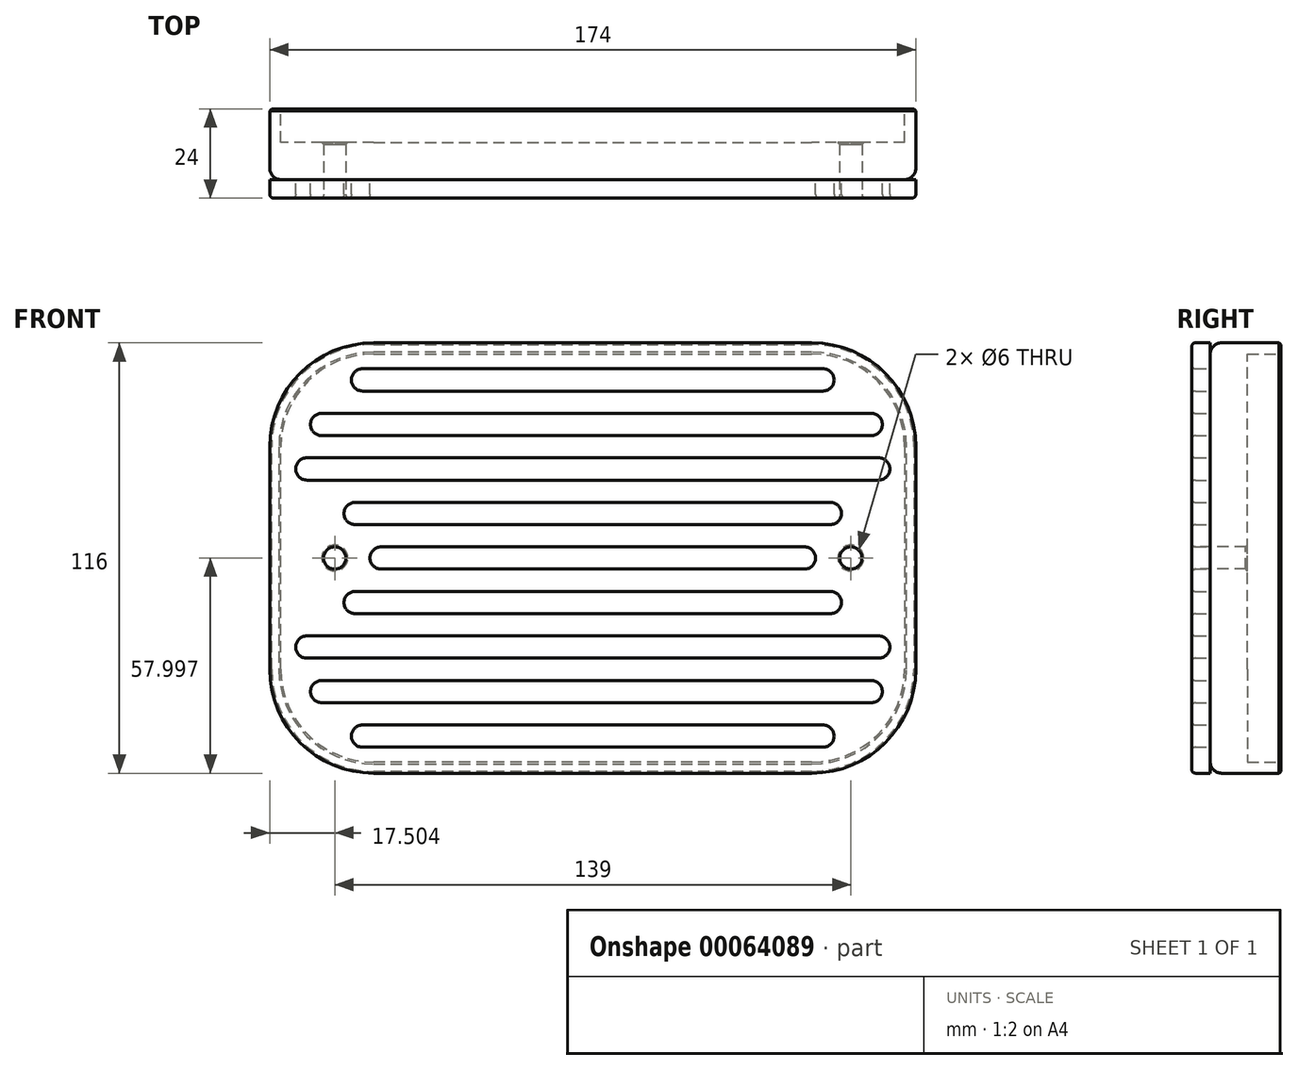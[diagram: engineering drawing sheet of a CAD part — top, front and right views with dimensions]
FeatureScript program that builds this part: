
annotation { "Feature Type Name" : "Feature", "Feature Type Description" : "" }
export const myFeature = defineFeature(function(context is Context, id is Id, definition is map)
    precondition{}
    {
        {
            var Q0;
            Q0=qCreatedBy(makeId("Front.planeOp"),FACE);
            var sketch = newSketch(context, id + "F0", { "sketchPlane" : qUnion([Q0])});
            skLineSegment(sketch, "E0.bottom", {"start": v(-55.39, -93.65) * mm, "end": v(62.61, -93.65) * mm});
            skLineSegment(sketch, "E0.top", {"start": v(-55.39, 16.35) * mm, "end": v(62.61, 16.35) * mm});
            skLineSegment(sketch, "E0.left", {"start": v(-80.39, -68.65) * mm, "end": v(-80.39, -8.65) * mm});
            skLineSegment(sketch, "E0.right", {"start": v(87.61, -68.65) * mm, "end": v(87.61, -8.65) * mm});
            skPoint(sketch, "E1.visualSharp", {"position": v(-80.39, 16.35) * mm});
            skArc(sketch, "E1.filletArc", {"start": v(-55.39, 16.35) * mm, "mid": v(-73.06, 9.02) * mm, "end": v(-80.39, -8.65) * mm});
            skPoint(sketch, "E2.visualSharp", {"position": v(87.61, 16.35) * mm});
            skArc(sketch, "E2.filletArc", {"start": v(87.61, -8.65) * mm, "mid": v(80.3, 9.02) * mm, "end": v(62.61, 16.35) * mm});
            skPoint(sketch, "E3.visualSharp", {"position": v(87.61, -93.65) * mm});
            skArc(sketch, "E3.filletArc", {"start": v(62.61, -93.65) * mm, "mid": v(80.3, -86.33) * mm, "end": v(87.61, -68.65) * mm});
            skPoint(sketch, "E4.visualSharp", {"position": v(-80.39, -93.65) * mm});
            skArc(sketch, "E4.filletArc", {"start": v(-80.39, -68.65) * mm, "mid": v(-73.06, -86.33) * mm, "end": v(-55.39, -93.65) * mm});
            skLineSegment(sketch, "E5.0", {"start": v(-55.39, 19.35) * mm, "end": v(62.61, 19.35) * mm});
            skArc(sketch, "E6.0", {"start": v(90.61, -8.65) * mm, "mid": v(82.41, 11.15) * mm, "end": v(62.61, 19.35) * mm});
            skLineSegment(sketch, "E6.1", {"start": v(90.61, -68.65) * mm, "end": v(90.61, -8.65) * mm});
            skArc(sketch, "E6.2", {"start": v(62.61, -96.65) * mm, "mid": v(82.41, -88.45) * mm, "end": v(90.61, -68.65) * mm});
            skArc(sketch, "E6.3", {"start": v(-55.39, 19.35) * mm, "mid": v(-75.19, 11.15) * mm, "end": v(-83.39, -8.65) * mm});
            skLineSegment(sketch, "E6.4", {"start": v(-83.39, -68.65) * mm, "end": v(-83.39, -8.65) * mm});
            skArc(sketch, "E6.5", {"start": v(-83.39, -68.65) * mm, "mid": v(-75.19, -88.45) * mm, "end": v(-55.39, -96.65) * mm});
            skLineSegment(sketch, "E6.6", {"start": v(-55.39, -96.65) * mm, "end": v(62.61, -96.65) * mm});
            skSolve(sketch);
        }
        {
            var Q0;
            Q0=makeQuery(id+"F0.imprint","IMPRINT",FACE,{"disambiguationData":[TD([[makeQuery(id+"F0.imprint","IMPRINT",EDGE,{"derivedFrom":sQuery(id+"F0.wireOp",EDGE,"E0.bottom")}),1.0]])]});
            var Q1;
            Q1=makeQuery(id+"F0.imprint","IMPRINT",FACE,{"disambiguationData":[TD([[makeQuery(id+"F0.imprint","IMPRINT",EDGE,{"derivedFrom":sQuery(id+"F0.wireOp",EDGE,"E0.bottom")}),-1.0]])]});
            extrude(context, id + "F1", {"entities" : qUnion([Q0, Q1]), "depth" : 19 * mm});
        }
        {
            var Q0;
            Q0=makeQuery(id+"F0.imprint","IMPRINT",FACE,{"disambiguationData":[TD([[makeQuery(id+"F0.imprint","IMPRINT",EDGE,{"derivedFrom":sQuery(id+"F0.wireOp",EDGE,"E0.bottom")}),1.0]])]});
            extrude(context, id + "F2", {"entities" : qUnion([Q0]), "operationType" : NewBodyOperationType.REMOVE, "depth" : 9 * mm});
        }
        {
            var Q0;
            Q0=makeQuery(id+"F1.opExtrude","CAP_FACE",FACE,{"disambiguationData":[OSD([sQuery(id+"F0.wireOp",EDGE,"E5.0"),sQuery(id+"F0.wireOp",EDGE,"E6.0"),sQuery(id+"F0.wireOp",EDGE,"E6.1"),sQuery(id+"F0.wireOp",EDGE,"E6.2"),sQuery(id+"F0.wireOp",EDGE,"E6.3"),sQuery(id+"F0.wireOp",EDGE,"E6.4"),sQuery(id+"F0.wireOp",EDGE,"E6.5"),sQuery(id+"F0.wireOp",EDGE,"E6.6")])],"isStart":false});
            var sketch = newSketch(context, id + "F3", { "sketchPlane" : qUnion([Q0])});
            skCircle(sketch, "E7", {"center": v(-65.89, -38.65) * mm, "radius": 3 * mm});
            skCircle(sketch, "E8", {"center": v(73.11, -38.65) * mm, "radius": 3 * mm});
            skLineSegment(sketch, "E9", {"start": v(-53.39, -38.65) * mm, "end": v(60.61, -38.65) * mm});
            skLineSegment(sketch, "E10.0", {"start": v(-60.39, -26.65) * mm, "end": v(67.61, -26.65) * mm});
            skLineSegment(sketch, "E11.0", {"start": v(-73.39, -14.65) * mm, "end": v(80.61, -14.65) * mm});
            skLineSegment(sketch, "E12.0", {"start": v(-69.39, -2.65) * mm, "end": v(78.61, -2.65) * mm});
            skLineSegment(sketch, "E13.0", {"start": v(-58.39, 9.35) * mm, "end": v(65.61, 9.35) * mm});
            skLineSegment(sketch, "E14.MirrorCS", {"start": v(-60.39, -50.65) * mm, "end": v(67.61, -50.65) * mm});
            skLineSegment(sketch, "E15.MirrorCS", {"start": v(-73.39, -62.65) * mm, "end": v(80.61, -62.65) * mm});
            skLineSegment(sketch, "E16.MirrorCS", {"start": v(-69.39, -74.65) * mm, "end": v(78.61, -74.65) * mm});
            skLineSegment(sketch, "E17.MirrorCS", {"start": v(-58.39, -86.65) * mm, "end": v(65.61, -86.65) * mm});
            skArc(sketch, "E18.0.startCap", {"start": v(-69.39, -5.65) * mm, "mid": v(-72.39, -2.65) * mm, "end": v(-69.39, 0.35) * mm});
            skArc(sketch, "E18.0.endCap", {"start": v(78.61, 0.35) * mm, "mid": v(81.61, -2.65) * mm, "end": v(78.61, -5.65) * mm});
            skLineSegment(sketch, "E18.0.left", {"start": v(-69.39, 0.35) * mm, "end": v(78.61, 0.35) * mm});
            skLineSegment(sketch, "E18.0.right", {"start": v(-69.39, -5.65) * mm, "end": v(78.61, -5.65) * mm});
            skArc(sketch, "E18.1.startCap", {"start": v(-73.39, -17.65) * mm, "mid": v(-76.39, -14.65) * mm, "end": v(-73.39, -11.65) * mm});
            skArc(sketch, "E18.1.endCap", {"start": v(80.61, -11.65) * mm, "mid": v(83.61, -14.65) * mm, "end": v(80.61, -17.65) * mm});
            skLineSegment(sketch, "E18.1.left", {"start": v(-73.39, -11.65) * mm, "end": v(80.61, -11.65) * mm});
            skLineSegment(sketch, "E18.1.right", {"start": v(-73.39, -17.65) * mm, "end": v(80.61, -17.65) * mm});
            skArc(sketch, "E18.2.startCap", {"start": v(-60.39, -29.65) * mm, "mid": v(-63.39, -26.65) * mm, "end": v(-60.39, -23.65) * mm});
            skArc(sketch, "E18.2.endCap", {"start": v(67.61, -23.65) * mm, "mid": v(70.61, -26.65) * mm, "end": v(67.61, -29.65) * mm});
            skLineSegment(sketch, "E18.2.left", {"start": v(-60.39, -23.65) * mm, "end": v(67.61, -23.65) * mm});
            skLineSegment(sketch, "E18.2.right", {"start": v(-60.39, -29.65) * mm, "end": v(67.61, -29.65) * mm});
            skArc(sketch, "E18.3.startCap", {"start": v(-53.39, -41.65) * mm, "mid": v(-56.39, -38.65) * mm, "end": v(-53.39, -35.65) * mm});
            skArc(sketch, "E18.3.endCap", {"start": v(60.61, -35.65) * mm, "mid": v(63.61, -38.65) * mm, "end": v(60.61, -41.65) * mm});
            skLineSegment(sketch, "E18.3.left", {"start": v(-53.39, -35.65) * mm, "end": v(60.61, -35.65) * mm});
            skLineSegment(sketch, "E18.3.right", {"start": v(-53.39, -41.65) * mm, "end": v(60.61, -41.65) * mm});
            skArc(sketch, "E18.4.startCap", {"start": v(-60.39, -53.65) * mm, "mid": v(-63.39, -50.65) * mm, "end": v(-60.39, -47.65) * mm});
            skArc(sketch, "E18.4.endCap", {"start": v(67.61, -47.65) * mm, "mid": v(70.61, -50.65) * mm, "end": v(67.61, -53.65) * mm});
            skLineSegment(sketch, "E18.4.left", {"start": v(-60.39, -47.65) * mm, "end": v(67.61, -47.65) * mm});
            skLineSegment(sketch, "E18.4.right", {"start": v(-60.39, -53.65) * mm, "end": v(67.61, -53.65) * mm});
            skArc(sketch, "E18.5.startCap", {"start": v(-73.39, -65.65) * mm, "mid": v(-76.39, -62.65) * mm, "end": v(-73.39, -59.65) * mm});
            skArc(sketch, "E18.5.endCap", {"start": v(80.61, -59.65) * mm, "mid": v(83.61, -62.65) * mm, "end": v(80.61, -65.65) * mm});
            skLineSegment(sketch, "E18.5.left", {"start": v(-73.39, -59.65) * mm, "end": v(80.61, -59.65) * mm});
            skLineSegment(sketch, "E18.5.right", {"start": v(-73.39, -65.65) * mm, "end": v(80.61, -65.65) * mm});
            skArc(sketch, "E18.6.startCap", {"start": v(-69.39, -77.65) * mm, "mid": v(-72.39, -74.65) * mm, "end": v(-69.39, -71.65) * mm});
            skArc(sketch, "E18.6.endCap", {"start": v(78.61, -71.65) * mm, "mid": v(81.61, -74.65) * mm, "end": v(78.61, -77.65) * mm});
            skLineSegment(sketch, "E18.6.left", {"start": v(-69.39, -71.65) * mm, "end": v(78.61, -71.65) * mm});
            skLineSegment(sketch, "E18.6.right", {"start": v(-69.39, -77.65) * mm, "end": v(78.61, -77.65) * mm});
            skArc(sketch, "E18.7.startCap", {"start": v(-58.39, -89.65) * mm, "mid": v(-61.39, -86.65) * mm, "end": v(-58.39, -83.65) * mm});
            skArc(sketch, "E18.7.endCap", {"start": v(65.61, -83.65) * mm, "mid": v(68.61, -86.65) * mm, "end": v(65.61, -89.65) * mm});
            skLineSegment(sketch, "E18.7.left", {"start": v(-58.39, -83.65) * mm, "end": v(65.61, -83.65) * mm});
            skLineSegment(sketch, "E18.7.right", {"start": v(-58.39, -89.65) * mm, "end": v(65.61, -89.65) * mm});
            skArc(sketch, "E18.8.startCap", {"start": v(-58.39, 6.35) * mm, "mid": v(-61.39, 9.35) * mm, "end": v(-58.39, 12.35) * mm});
            skArc(sketch, "E18.8.endCap", {"start": v(65.61, 12.35) * mm, "mid": v(68.61, 9.35) * mm, "end": v(65.61, 6.35) * mm});
            skLineSegment(sketch, "E18.8.left", {"start": v(-58.39, 12.35) * mm, "end": v(65.61, 12.35) * mm});
            skLineSegment(sketch, "E18.8.right", {"start": v(-58.39, 6.35) * mm, "end": v(65.61, 6.35) * mm});
            skSolve(sketch);
        }
        {
            var Q0;
            Q0=makeQuery(id+"F3.imprint","IMPRINT",FACE,{"disambiguationData":[TD([[makeQuery(id+"F3.imprint","IMPRINT",EDGE,{"derivedFrom":sQuery(id+"F3.wireOp",EDGE,"E7")}),1.0]])]});
            var Q1;
            Q1=makeQuery(id+"F3.imprint","IMPRINT",FACE,{"disambiguationData":[TD([[makeQuery(id+"F3.imprint","IMPRINT",EDGE,{"derivedFrom":sQuery(id+"F3.wireOp",EDGE,"E8")}),1.0]])]});
            extrude(context, id + "F4", {"entities" : qUnion([Q0, Q1]), "operationType" : NewBodyOperationType.REMOVE, "endBound" : BoundingType.THROUGH_ALL, "oppositeDirection" : true, "depth" : 25 * mm});
        }
        {
            var Q0;
            Q0=makeQuery(id+"F1.opExtrude","CAP_EDGE",EDGE,{"disambiguationData":[OSD([sQuery(id+"F0.wireOp",EDGE,"E6.3")])],"isStart":false});
            var Q1;
            Q1=makeQuery(id+"F1.opExtrude","CAP_EDGE",EDGE,{"disambiguationData":[OSD([sQuery(id+"F0.wireOp",EDGE,"E5.0")])],"isStart":false});
            var Q2;
            Q2=makeQuery(id+"F1.opExtrude","CAP_EDGE",EDGE,{"disambiguationData":[OSD([sQuery(id+"F0.wireOp",EDGE,"E6.0")])],"isStart":false});
            var Q3;
            Q3=makeQuery(id+"F1.opExtrude","CAP_EDGE",EDGE,{"disambiguationData":[OSD([sQuery(id+"F0.wireOp",EDGE,"E6.1")])],"isStart":false});
            var Q4;
            Q4=makeQuery(id+"F1.opExtrude","CAP_EDGE",EDGE,{"disambiguationData":[OSD([sQuery(id+"F0.wireOp",EDGE,"E6.2")])],"isStart":false});
            var Q5;
            Q5=makeQuery(id+"F1.opExtrude","CAP_EDGE",EDGE,{"disambiguationData":[OSD([sQuery(id+"F0.wireOp",EDGE,"E6.6")])],"isStart":false});
            var Q6;
            Q6=makeQuery(id+"F1.opExtrude","CAP_EDGE",EDGE,{"disambiguationData":[OSD([sQuery(id+"F0.wireOp",EDGE,"E6.5")])],"isStart":false});
            var Q7;
            Q7=makeQuery(id+"F1.opExtrude","CAP_EDGE",EDGE,{"disambiguationData":[OSD([sQuery(id+"F0.wireOp",EDGE,"E6.4")])],"isStart":false});
            var Q8;
            Q8=makeQuery(id+"F1.opExtrude","CAP_EDGE",EDGE,{"disambiguationData":[OSD([sQuery(id+"F0.wireOp",EDGE,"E6.5")])],"isStart":false});
            fillet(context, id + "F5", {"entities" : qUnion([Q0, Q1, Q2, Q3, Q4, Q5, Q6, Q7, Q8]), "radius" : 3 * mm, "tangentPropagation" : true, "allowEdgeOverflow" : false});
        }
        {
            var Q0;
            Q0=makeQuery(id+"F4.boolean.opBoolean","COPY",EDGE,{"derivedFrom":makeQuery(id+"F4.opExtrude","CAP_EDGE",EDGE,{"disambiguationData":[OSD([sQuery(id+"F3.wireOp",EDGE,"E7")])],"isStart":true})});
            var Q1;
            Q1=makeQuery(id+"F4.boolean.opBoolean","INTERSECT",EDGE,{"derivedFrom":[makeQuery(id+"F2.boolean.opBoolean","COPY",FACE,{"derivedFrom":makeQuery(id+"F2.opExtrude","CAP_FACE",FACE,{"disambiguationData":[OSD([sQuery(id+"F0.wireOp",EDGE,"E0.bottom"),sQuery(id+"F0.wireOp",EDGE,"E0.top"),sQuery(id+"F0.wireOp",EDGE,"E0.left"),sQuery(id+"F0.wireOp",EDGE,"E0.right"),sQuery(id+"F0.wireOp",EDGE,"E1.filletArc"),sQuery(id+"F0.wireOp",EDGE,"E2.filletArc"),sQuery(id+"F0.wireOp",EDGE,"E3.filletArc"),sQuery(id+"F0.wireOp",EDGE,"E4.filletArc")])],"isStart":false})}),makeQuery(id+"F4.opExtrude","SWEPT_FACE",FACE,{"disambiguationData":[OSD([sQuery(id+"F3.wireOp",EDGE,"E8")])]})]});
            var Q2;
            Q2=makeQuery(id+"F4.boolean.opBoolean","INTERSECT",EDGE,{"derivedFrom":[makeQuery(id+"F2.boolean.opBoolean","COPY",FACE,{"derivedFrom":makeQuery(id+"F2.opExtrude","CAP_FACE",FACE,{"disambiguationData":[OSD([sQuery(id+"F0.wireOp",EDGE,"E0.bottom"),sQuery(id+"F0.wireOp",EDGE,"E0.top"),sQuery(id+"F0.wireOp",EDGE,"E0.left"),sQuery(id+"F0.wireOp",EDGE,"E0.right"),sQuery(id+"F0.wireOp",EDGE,"E1.filletArc"),sQuery(id+"F0.wireOp",EDGE,"E2.filletArc"),sQuery(id+"F0.wireOp",EDGE,"E3.filletArc"),sQuery(id+"F0.wireOp",EDGE,"E4.filletArc")])],"isStart":false})}),makeQuery(id+"F4.opExtrude","SWEPT_FACE",FACE,{"disambiguationData":[OSD([sQuery(id+"F3.wireOp",EDGE,"E7")])]})]});
            var Q3;
            Q3=makeQuery(id+"F4.boolean.opBoolean","COPY",EDGE,{"derivedFrom":makeQuery(id+"F4.opExtrude","CAP_EDGE",EDGE,{"disambiguationData":[OSD([sQuery(id+"F3.wireOp",EDGE,"E8")])],"isStart":true})});
            chamfer(context, id + "F6", {"entities" : qUnion([Q0, Q1, Q2, Q3]), "width" : 0.5 * mm, "tangentPropagation" : true});
        }
        {
            var Q0;
            Q0=makeQuery(id+"F1.opExtrude","CAP_FACE",FACE,{"disambiguationData":[OSD([sQuery(id+"F0.wireOp",EDGE,"E5.0"),sQuery(id+"F0.wireOp",EDGE,"E6.0"),sQuery(id+"F0.wireOp",EDGE,"E6.1"),sQuery(id+"F0.wireOp",EDGE,"E6.2"),sQuery(id+"F0.wireOp",EDGE,"E6.3"),sQuery(id+"F0.wireOp",EDGE,"E6.4"),sQuery(id+"F0.wireOp",EDGE,"E6.5"),sQuery(id+"F0.wireOp",EDGE,"E6.6")])],"isStart":true});
            chamfer(context, id + "F7", {"entities" : qUnion([Q0]), "width" : 0.5 * mm, "tangentPropagation" : true});
        }
        {
            var Q0;
            Q0=makeQuery(id+"F3.imprint","IMPRINT",FACE,{"disambiguationData":[TD([[makeQuery(id+"F3.imprint","IMPRINT",EDGE,{"derivedFrom":sQuery(id+"F3.wireOp",EDGE,"E18.8.startCap")}),-1.0]])]});
            var Q1;
            Q1=makeQuery(id+"F3.imprint","IMPRINT",FACE,{"disambiguationData":[TD([[makeQuery(id+"F3.imprint","IMPRINT",EDGE,{"derivedFrom":sQuery(id+"F3.wireOp",EDGE,"E18.0.startCap")}),-1.0]])]});
            var Q2;
            Q2=makeQuery(id+"F3.imprint","IMPRINT",FACE,{"disambiguationData":[TD([[makeQuery(id+"F3.imprint","IMPRINT",EDGE,{"derivedFrom":sQuery(id+"F3.wireOp",EDGE,"E18.1.startCap")}),-1.0]])]});
            var Q3;
            Q3=makeQuery(id+"F3.imprint","IMPRINT",FACE,{"disambiguationData":[TD([[makeQuery(id+"F3.imprint","IMPRINT",EDGE,{"derivedFrom":sQuery(id+"F3.wireOp",EDGE,"E18.2.startCap")}),-1.0]])]});
            var Q4;
            Q4=makeQuery(id+"F3.imprint","IMPRINT",FACE,{"disambiguationData":[TD([[makeQuery(id+"F3.imprint","IMPRINT",EDGE,{"derivedFrom":sQuery(id+"F3.wireOp",EDGE,"E18.3.startCap")}),-1.0]])]});
            var Q5;
            Q5=makeQuery(id+"F3.imprint","IMPRINT",FACE,{"disambiguationData":[TD([[makeQuery(id+"F3.imprint","IMPRINT",EDGE,{"derivedFrom":sQuery(id+"F3.wireOp",EDGE,"E18.4.startCap")}),-1.0]])]});
            var Q6;
            Q6=makeQuery(id+"F3.imprint","IMPRINT",FACE,{"disambiguationData":[TD([[makeQuery(id+"F3.imprint","IMPRINT",EDGE,{"derivedFrom":sQuery(id+"F3.wireOp",EDGE,"E18.5.startCap")}),-1.0]])]});
            var Q7;
            Q7=makeQuery(id+"F3.imprint","IMPRINT",FACE,{"disambiguationData":[TD([[makeQuery(id+"F3.imprint","IMPRINT",EDGE,{"derivedFrom":sQuery(id+"F3.wireOp",EDGE,"E18.6.startCap")}),-1.0]])]});
            var Q8;
            Q8=makeQuery(id+"F3.imprint","IMPRINT",FACE,{"disambiguationData":[TD([[makeQuery(id+"F3.imprint","IMPRINT",EDGE,{"derivedFrom":sQuery(id+"F3.wireOp",EDGE,"E18.7.startCap")}),-1.0]])]});
            extrude(context, id + "F8", {"entities" : qUnion([Q0, Q1, Q2, Q3, Q4, Q5, Q6, Q7, Q8]), "operationType" : NewBodyOperationType.ADD, "depth" : 5 * mm});
        }
        {
            var Q0;
            Q0=makeQuery(id+"F8.opExtrude","CAP_FACE",FACE,{"disambiguationData":[OSD([sQuery(id+"F3.wireOp",EDGE,"E18.8.startCap"),sQuery(id+"F3.wireOp",EDGE,"E18.8.endCap"),sQuery(id+"F3.wireOp",EDGE,"E18.8.left"),sQuery(id+"F3.wireOp",EDGE,"E18.8.right")])],"isStart":false});
            var Q1;
            Q1=makeQuery(id+"F8.opExtrude","CAP_FACE",FACE,{"disambiguationData":[OSD([sQuery(id+"F3.wireOp",EDGE,"E18.0.startCap"),sQuery(id+"F3.wireOp",EDGE,"E18.0.endCap"),sQuery(id+"F3.wireOp",EDGE,"E18.0.left"),sQuery(id+"F3.wireOp",EDGE,"E18.0.right")])],"isStart":false});
            var Q2;
            Q2=makeQuery(id+"F8.opExtrude","CAP_FACE",FACE,{"disambiguationData":[OSD([sQuery(id+"F3.wireOp",EDGE,"E18.1.startCap"),sQuery(id+"F3.wireOp",EDGE,"E18.1.endCap"),sQuery(id+"F3.wireOp",EDGE,"E18.1.left"),sQuery(id+"F3.wireOp",EDGE,"E18.1.right")])],"isStart":false});
            var Q3;
            Q3=makeQuery(id+"F8.opExtrude","CAP_FACE",FACE,{"disambiguationData":[OSD([sQuery(id+"F3.wireOp",EDGE,"E18.2.startCap"),sQuery(id+"F3.wireOp",EDGE,"E18.2.endCap"),sQuery(id+"F3.wireOp",EDGE,"E18.2.left"),sQuery(id+"F3.wireOp",EDGE,"E18.2.right")])],"isStart":false});
            var Q4;
            Q4=makeQuery(id+"F8.opExtrude","CAP_FACE",FACE,{"disambiguationData":[OSD([sQuery(id+"F3.wireOp",EDGE,"E18.3.startCap"),sQuery(id+"F3.wireOp",EDGE,"E18.3.endCap"),sQuery(id+"F3.wireOp",EDGE,"E18.3.left"),sQuery(id+"F3.wireOp",EDGE,"E18.3.right")])],"isStart":false});
            var Q5;
            Q5=makeQuery(id+"F8.opExtrude","CAP_FACE",FACE,{"disambiguationData":[OSD([sQuery(id+"F3.wireOp",EDGE,"E18.4.startCap"),sQuery(id+"F3.wireOp",EDGE,"E18.4.endCap"),sQuery(id+"F3.wireOp",EDGE,"E18.4.left"),sQuery(id+"F3.wireOp",EDGE,"E18.4.right")])],"isStart":false});
            var Q6;
            Q6=makeQuery(id+"F8.opExtrude","CAP_FACE",FACE,{"disambiguationData":[OSD([sQuery(id+"F3.wireOp",EDGE,"E18.5.startCap"),sQuery(id+"F3.wireOp",EDGE,"E18.5.endCap"),sQuery(id+"F3.wireOp",EDGE,"E18.5.left"),sQuery(id+"F3.wireOp",EDGE,"E18.5.right")])],"isStart":false});
            var Q7;
            Q7=makeQuery(id+"F8.opExtrude","CAP_FACE",FACE,{"disambiguationData":[OSD([sQuery(id+"F3.wireOp",EDGE,"E18.6.startCap"),sQuery(id+"F3.wireOp",EDGE,"E18.6.endCap"),sQuery(id+"F3.wireOp",EDGE,"E18.6.left"),sQuery(id+"F3.wireOp",EDGE,"E18.6.right")])],"isStart":false});
            var Q8;
            Q8=makeQuery(id+"F8.opExtrude","CAP_FACE",FACE,{"disambiguationData":[OSD([sQuery(id+"F3.wireOp",EDGE,"E18.7.startCap"),sQuery(id+"F3.wireOp",EDGE,"E18.7.endCap"),sQuery(id+"F3.wireOp",EDGE,"E18.7.left"),sQuery(id+"F3.wireOp",EDGE,"E18.7.right")])],"isStart":false});
            fillet(context, id + "F9", {"entities" : qUnion([Q0, Q1, Q2, Q3, Q4, Q5, Q6, Q7, Q8]), "radius" : 1 * mm, "tangentPropagation" : true, "allowEdgeOverflow" : false});
        }
    });
